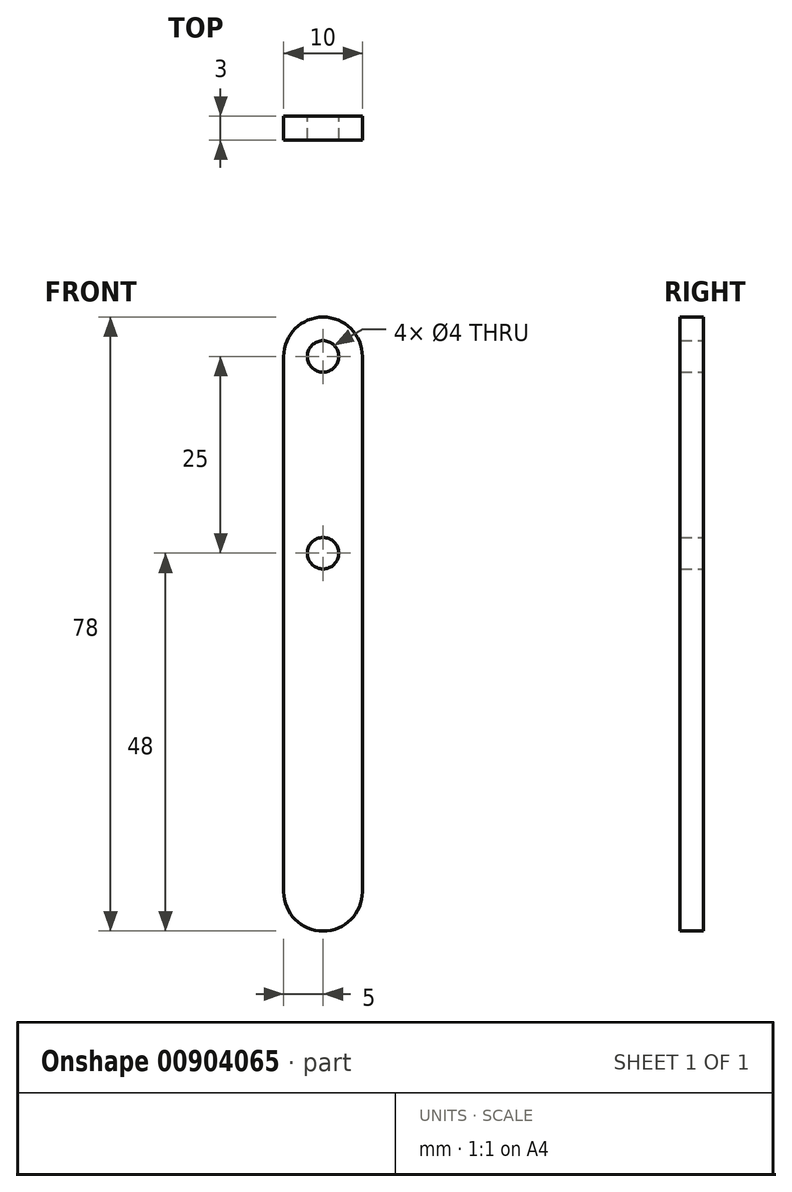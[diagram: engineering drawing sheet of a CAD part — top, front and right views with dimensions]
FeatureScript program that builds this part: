
annotation { "Feature Type Name" : "Feature", "Feature Type Description" : "" }
export const myFeature = defineFeature(function(context is Context, id is Id, definition is map)
    precondition{}
    {
        {
            var Q0;
            Q0=qCreatedBy(makeId("Front.planeOp"),FACE);
            var sketch = newSketch(context, id + "F0", { "sketchPlane" : qUnion([Q0])});
            skArc(sketch, "E0", {"start": v(-5, 0) * mm, "mid": v(0, -5) * mm, "end": v(5, 0) * mm});
            skArc(sketch, "E1", {"start": v(5, 68) * mm, "mid": v(0, 73) * mm, "end": v(-5, 68) * mm});
            skLineSegment(sketch, "E2", {"start": v(-5, 68) * mm, "end": v(-5, 0) * mm});
            skLineSegment(sketch, "E3.MirrorCS", {"start": v(5, 68) * mm, "end": v(5, 0) * mm});
            skCircle(sketch, "E4", {"center": v(0, 68) * mm, "radius": 2 * mm});
            skCircle(sketch, "E5", {"center": v(0, 43) * mm, "radius": 2 * mm});
            skSolve(sketch);
        }
        {
            var Q0;
            Q0 = qSketchRegion(id + "F0", true);
            extrude(context, id + "F1", {"entities" : qUnion([Q0]), "depth" : 3 * mm, "offsetDistance" : 25 * mm});
        }
    });
